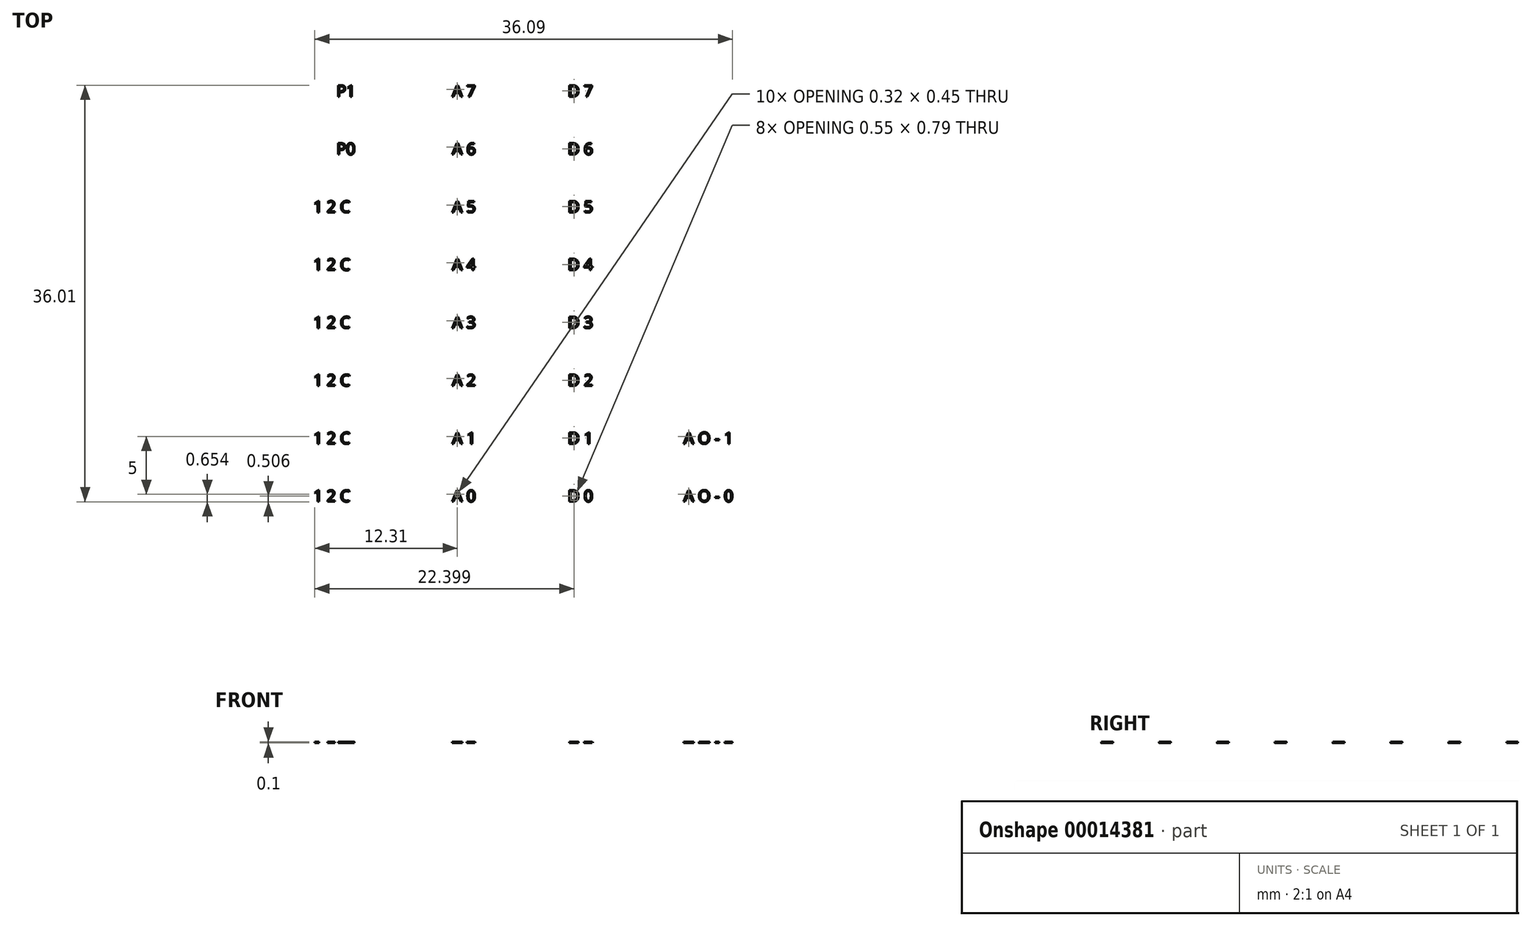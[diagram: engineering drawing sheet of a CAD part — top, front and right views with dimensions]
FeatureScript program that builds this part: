
annotation { "Feature Type Name" : "Feature", "Feature Type Description" : "" }
export const myFeature = defineFeature(function(context is Context, id is Id, definition is map)
    precondition{}
    {
        {
            var Q0;
            Q0=qCreatedBy(makeId("Top.planeOp"),FACE);
            var sketch = newSketch(context, id + "F0", { "sketchPlane" : qUnion([Q0])});
            skText(sketch, "E0", { "text": "P1", "fontName": "OpenSans-Regular.ttf"});
            skPoint(sketch, "E1", {"position": v(0, 0) * mm});
            skPoint(sketch, "E2.0.1.0", {"position": v(0, -5) * mm});
            skPoint(sketch, "E2.0.1.1", {"position": v(0, -5) * mm});
            skPoint(sketch, "E2.0.1.2", {"position": v(0, -5) * mm});
            skPoint(sketch, "E2.1.0.0", {"position": v(10, 0) * mm});
            skPoint(sketch, "E2.1.0.1", {"position": v(10, 0) * mm});
            skPoint(sketch, "E2.1.0.2", {"position": v(10, 0) * mm});
            skPoint(sketch, "E2.1.1.0", {"position": v(10, -5) * mm});
            skPoint(sketch, "E2.1.1.1", {"position": v(10, -5) * mm});
            skPoint(sketch, "E2.1.1.2", {"position": v(10, -5) * mm});
            skPoint(sketch, "E2.2.0.0", {"position": v(20, 0) * mm});
            skPoint(sketch, "E2.2.0.1", {"position": v(20, 0) * mm});
            skPoint(sketch, "E2.2.0.2", {"position": v(20, 0) * mm});
            skPoint(sketch, "E2.2.1.0", {"position": v(20, -5) * mm});
            skPoint(sketch, "E2.2.1.1", {"position": v(20, -5) * mm});
            skPoint(sketch, "E2.2.1.2", {"position": v(20, -5) * mm});
            skLineSegment(sketch, "E2.direction1", {"start": v(0, 0) * mm, "end": v(10, 0) * mm, "construction": true});
            skLineSegment(sketch, "E2.direction2", {"start": v(0, 0) * mm, "end": v(0, -5) * mm, "construction": true});
            skText(sketch, "E3", { "text": "A 7", "fontName": "OpenSans-Regular.ttf"});
            skText(sketch, "E4", { "text": "D 7", "fontName": "OpenSans-Regular.ttf"});
            skText(sketch, "E5", { "text": "P0", "fontName": "OpenSans-Regular.ttf"});
            skText(sketch, "E6", { "text": "A 6\n", "fontName": "OpenSans-Regular.ttf"});
            skText(sketch, "E7", { "text": "D 6\n", "fontName": "OpenSans-Regular.ttf"});
            skText(sketch, "E8", { "text": "1 2 C", "fontName": "OpenSans-Regular.ttf"});
            skPoint(sketch, "E9", {"position": v(-2, -10) * mm});
            skPoint(sketch, "E10.0.1.0", {"position": v(10, -10) * mm});
            skPoint(sketch, "E10.0.1.1", {"position": v(20, -10) * mm});
            skPoint(sketch, "E10.0.2.0", {"position": v(10, -15) * mm});
            skPoint(sketch, "E10.0.2.1", {"position": v(20, -15) * mm});
            skPoint(sketch, "E10.0.3.0", {"position": v(10, -20) * mm});
            skPoint(sketch, "E10.0.3.1", {"position": v(20, -20) * mm});
            skPoint(sketch, "E10.0.4.0", {"position": v(10, -25) * mm});
            skPoint(sketch, "E10.0.4.1", {"position": v(20, -25) * mm});
            skPoint(sketch, "E10.0.5.0", {"position": v(10, -30) * mm});
            skPoint(sketch, "E10.0.5.1", {"position": v(20, -30) * mm});
            skPoint(sketch, "E10.0.6.0", {"position": v(10, -35) * mm});
            skPoint(sketch, "E10.0.6.1", {"position": v(20, -35) * mm});
            skLineSegment(sketch, "E10.direction1", {"start": v(10, -5) * mm, "end": v(25.41, -5) * mm, "construction": true});
            skLineSegment(sketch, "E10.direction2", {"start": v(10, -5) * mm, "end": v(10, -10) * mm, "construction": true});
            skPoint(sketch, "E11.0.1.0", {"position": v(-2, -15) * mm});
            skPoint(sketch, "E11.0.2.0", {"position": v(-2, -20) * mm});
            skPoint(sketch, "E11.0.3.0", {"position": v(-2, -25) * mm});
            skPoint(sketch, "E11.0.4.0", {"position": v(-2, -30) * mm});
            skPoint(sketch, "E11.0.5.0", {"position": v(-2, -35) * mm});
            skLineSegment(sketch, "E11.direction1", {"start": v(-2, -10) * mm, "end": v(23, -10) * mm, "construction": true});
            skLineSegment(sketch, "E11.direction2", {"start": v(-2, -10) * mm, "end": v(-2, -15) * mm, "construction": true});
            skText(sketch, "E12", { "text": "1 2 C", "fontName": "OpenSans-Regular.ttf"});
            skText(sketch, "E13", { "text": "1 2 C", "fontName": "OpenSans-Regular.ttf"});
            skText(sketch, "E14", { "text": "1 2 C", "fontName": "OpenSans-Regular.ttf"});
            skText(sketch, "E15", { "text": "1 2 C", "fontName": "OpenSans-Regular.ttf"});
            skText(sketch, "E16", { "text": "1 2 C", "fontName": "OpenSans-Regular.ttf"});
            skText(sketch, "E17", { "text": "A 5", "fontName": "OpenSans-Regular.ttf"});
            skText(sketch, "E18", { "text": "A 4\n", "fontName": "OpenSans-Regular.ttf"});
            skText(sketch, "E19", { "text": "A 3", "fontName": "OpenSans-Regular.ttf"});
            skText(sketch, "E20", { "text": "A 2\n", "fontName": "OpenSans-Regular.ttf"});
            skText(sketch, "E21", { "text": "A 1", "fontName": "OpenSans-Regular.ttf"});
            skText(sketch, "E22", { "text": "A 0", "fontName": "OpenSans-Regular.ttf"});
            skText(sketch, "E23", { "text": "D 5", "fontName": "OpenSans-Regular.ttf"});
            skText(sketch, "E24", { "text": "D 4\n", "fontName": "OpenSans-Regular.ttf"});
            skText(sketch, "E25", { "text": "D 3\n", "fontName": "OpenSans-Regular.ttf"});
            skText(sketch, "E26", { "text": "D 2\n", "fontName": "OpenSans-Regular.ttf"});
            skText(sketch, "E27", { "text": "D 1\n", "fontName": "OpenSans-Regular.ttf"});
            skText(sketch, "E28", { "text": "D 0\n", "fontName": "OpenSans-Regular.ttf"});
            skPoint(sketch, "E29.1.0.0", {"position": v(30, -30) * mm});
            skPoint(sketch, "E29.1.0.1", {"position": v(30, -35) * mm});
            skPoint(sketch, "E29.1.1.0", {"position": v(30, -35) * mm});
            skLineSegment(sketch, "E29.direction1", {"start": v(20, -30) * mm, "end": v(30, -30) * mm, "construction": true});
            skLineSegment(sketch, "E29.direction2", {"start": v(20, -30) * mm, "end": v(20, -35) * mm, "construction": true});
            skText(sketch, "E30", { "text": "A O - 1", "fontName": "OpenSans-Regular.ttf"});
            skText(sketch, "E31", { "text": "A O - 0", "fontName": "OpenSans-Regular.ttf"});
            const initialGuessF0  = {"E0": [0, -0.001, 1, 0, 0.001], "E3": [0.01, -0.001, 1, 0, 0.001], "E4": [0.02, -0.001, 1, 0, 0.001], "E5": [0, -0.006, 1, 0, 0.001], "E6": [0.01, -0.006, 1, 0, 0.001], "E7": [0.02, -0.006, 1, 0, 0.001], "E8": [-0.002, -0.011, 1, 0, 0.001], "E12": [-0.002, -0.016, 1, 0, 0.001], "E13": [-0.002, -0.021, 1, 0, 0.001], "E14": [-0.002, -0.026, 1, 0, 0.001], "E15": [-0.002, -0.031, 1, 0, 0.001], "E16": [-0.002, -0.036, 1, 0, 0.001], "E17": [0.01, -0.011, 1, 0, 0.001], "E18": [0.01, -0.016, 1, 0, 0.001], "E19": [0.01, -0.021, 1, 0, 0.001], "E20": [0.01, -0.026, 1, 0, 0.001], "E21": [0.01, -0.031, 1, 0, 0.001], "E22": [0.01, -0.036, 1, 0, 0.001], "E23": [0.02, -0.011, 1, 0, 0.001], "E24": [0.02, -0.016, 1, 0, 0.001], "E25": [0.02, -0.021, 1, 0, 0.001], "E26": [0.02, -0.026, 1, 0, 0.001], "E27": [0.02, -0.031, 1, 0, 0.001], "E28": [0.02, -0.036, 1, 0, 0.001], "E30": [0.03, -0.031, 1, 0, 0.001], "E31": [0.03, -0.036, 1, 0, 0.001]};
            skSetInitialGuess(sketch, initialGuessF0);
            skSolve(sketch);
        }
        {
            var Q0;
            Q0=qSketchRegion(id+"F0",true);
            extrude(context, id + "F1", {"entities" : qUnion([Q0]), "depth" : .1 * mm});
        }
    });
